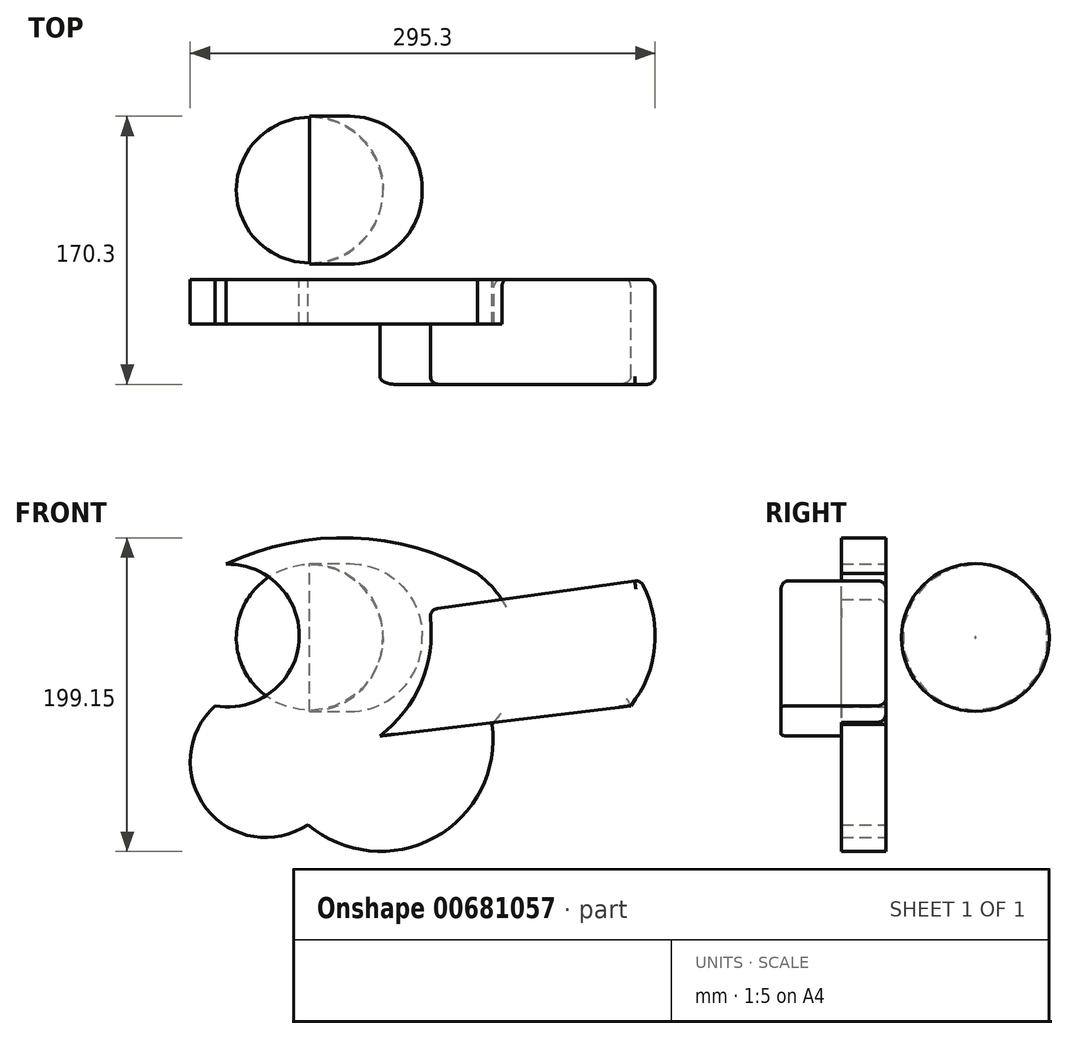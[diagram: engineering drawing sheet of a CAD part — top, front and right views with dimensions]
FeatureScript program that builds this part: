
annotation { "Feature Type Name" : "Feature", "Feature Type Description" : "" }
export const myFeature = defineFeature(function(context is Context, id is Id, definition is map)
    precondition{}
    {
        {
            var Q0;
            Q0=qCreatedBy(makeId("Front.planeOp"),FACE);
            var sketch = newSketch(context, id + "F0", { "sketchPlane" : qUnion([Q0])});
            skLineSegment(sketch, "E0", {"start": v(-71.36, -19.2) * mm, "end": v(88.05, 0) * mm});
            skLineSegment(sketch, "E1", {"start": v(-39.95, 61.02) * mm, "end": v(94.02, 79.81) * mm});
            skArc(sketch, "E2", {"start": v(-71.36, -19.2) * mm, "mid": v(-44.4, 16.5) * mm, "end": v(-39.95, 61.02) * mm});
            skArc(sketch, "E3", {"start": v(88.05, 0) * mm, "mid": v(103.29, 39) * mm, "end": v(94.02, 79.81) * mm});
            skSolve(sketch);
        }
        {
            var Q0;
            Q0 = qSketchRegion(id + "F0", true);
            extrude(context, id + "F1", {"entities" : qUnion([Q0]), "depth" : 66.55 * mm, "offsetDistance" : 25.4 * mm});
        }
        {
            var Q0;
            Q0=makeQuery(id+"F1.opExtrude","CAP_EDGE",EDGE,{"disambiguationData":[OSD([sQuery(id+"F0.wireOp",EDGE,"E1")])],"isStart":false});
            fillet(context, id + "F2", {"entities" : qUnion([Q0]), "radius" : 5.08 * mm, "tangentPropagation" : true, "allowEdgeOverflow" : false});
        }
        {
            var Q0;
            Q0=makeQuery(id+"F1.opExtrude","CAP_EDGE",EDGE,{"disambiguationData":[OSD([sQuery(id+"F0.wireOp",EDGE,"E2")])],"isStart":false});
            var Q1;
            Q1=makeQuery(id+"F1.opExtrude","CAP_EDGE",EDGE,{"disambiguationData":[OSD([sQuery(id+"F0.wireOp",EDGE,"E3")])],"isStart":false});
            fillet(context, id + "F3", {"entities" : qUnion([Q0, Q1]), "radius" : 5.08 * mm, "tangentPropagation" : true, "allowEdgeOverflow" : false});
        }
        {
            var Q0;
            Q0=makeQuery(id+"F1.opExtrude","CAP_FACE",FACE,{"disambiguationData":[OSD([sQuery(id+"F0.wireOp",EDGE,"E0"),sQuery(id+"F0.wireOp",EDGE,"E1"),sQuery(id+"F0.wireOp",EDGE,"E2"),sQuery(id+"F0.wireOp",EDGE,"E3")])],"isStart":true});
            fillet(context, id + "F4", {"entities" : qUnion([Q0]), "radius" : 5.08 * mm, "tangentPropagation" : true, "allowEdgeOverflow" : false});
        }
        {
            var Q0;
            Q0=qCreatedBy(makeId("Right.planeOp"),FACE);
            var sketch = newSketch(context, id + "F5", { "sketchPlane" : qUnion([Q0])});
            skCircle(sketch, "E4", {"center": v(56.8, 43.35) * mm, "radius": 46.95 * mm});
            skSolve(sketch);
        }
        {
            var Q0;
            Q0 = qSketchRegion(id + "F5", true);
            extrude(context, id + "F6", {"entities" : qUnion([Q0]), "oppositeDirection" : true, "depth" : 162.56 * mm, "offsetDistance" : 25.4 * mm});
        }
        {
            var Q0;
            Q0=makeQuery(id+"F6.opExtrude","CAP_FACE",FACE,{"disambiguationData":[OSD([sQuery(id+"F5.wireOp",EDGE,"E4")])],"isStart":false});
            fillet(context, id + "F7", {"entities" : qUnion([Q0]), "radius" : 46.6 * mm, "tangentPropagation" : true, "allowEdgeOverflow" : false});
        }
        {
            var Q0;
            Q0=makeQuery(id+"F6.opExtrude","CAP_FACE",FACE,{"disambiguationData":[OSD([sQuery(id+"F5.wireOp",EDGE,"E4")])],"isStart":true});
            extrude(context, id + "F8", {"entities" : qUnion([Q0]), "operationType" : NewBodyOperationType.REMOVE, "oppositeDirection" : true, "depth" : 44.45 * mm, "offsetDistance" : 25.4 * mm});
        }
        {
            var Q0;
            Q0=makeQuery(id+"F8.boolean.opBoolean","COPY",FACE,{"derivedFrom":makeQuery(id+"F8.opExtrude","CAP_FACE",FACE,{"disambiguationData":[OSD([sQuery(id+"F5.wireOp",EDGE,"E4")])],"isStart":false})});
            fillet(context, id + "F9", {"entities" : qUnion([Q0]), "radius" : 46 * mm, "tangentPropagation" : true, "allowEdgeOverflow" : false});
        }
        {
            var Q0;
            Q0=qCreatedBy(makeId("Front.planeOp"),FACE);
            var sketch = newSketch(context, id + "F10", { "sketchPlane" : qUnion([Q0])});
            skArc(sketch, "E5", {"start": v(-175.96, 0) * mm, "mid": v(-122.72, 41.12) * mm, "end": v(-169, 89.94) * mm});
            skArc(sketch, "E6", {"start": v(-9.4, 83.93) * mm, "mid": v(-88.46, 106.57) * mm, "end": v(-169, 89.94) * mm});
            skArc(sketch, "E7", {"start": v(0, -11.74) * mm, "mid": v(16.47, 38.18) * mm, "end": v(-9.4, 83.93) * mm});
            skArc(sketch, "E8", {"start": v(-117.05, -75.54) * mm, "mid": v(-36.67, -83.74) * mm, "end": v(0, -11.74) * mm});
            skArc(sketch, "E9", {"start": v(-175.96, 0) * mm, "mid": v(-181.67, -65.2) * mm, "end": v(-117.05, -75.54) * mm});
            skSolve(sketch);
        }
        {
            var Q0;
            Q0 = qSketchRegion(id + "F10", true);
            extrude(context, id + "F11", {"entities" : qUnion([Q0]), "operationType" : NewBodyOperationType.ADD, "depth" : 28.2 * mm, "offsetDistance" : 25.4 * mm});
        }
    });
